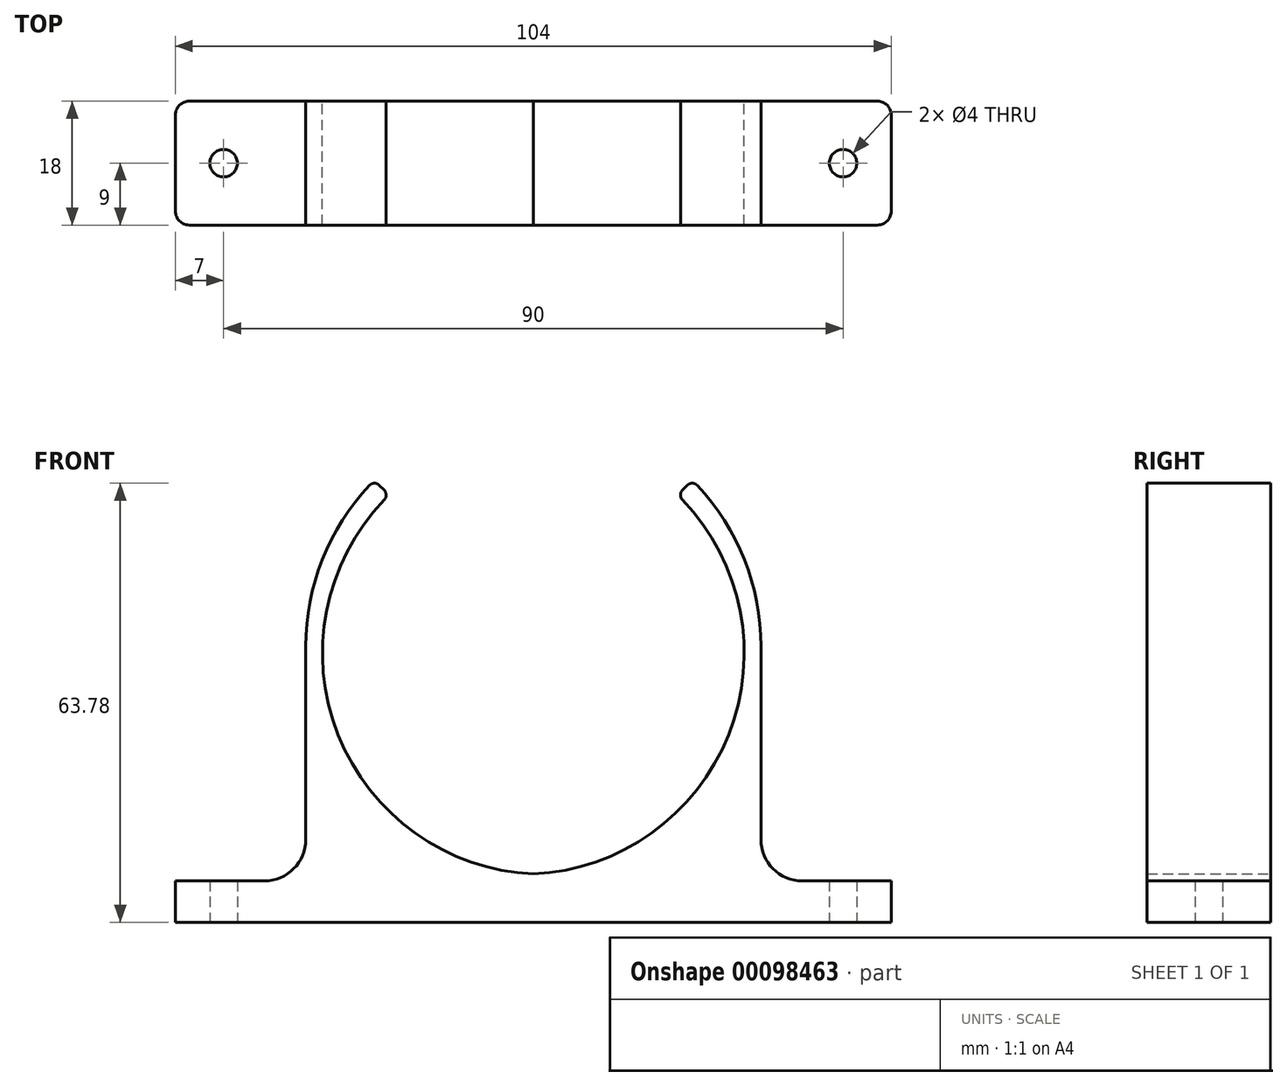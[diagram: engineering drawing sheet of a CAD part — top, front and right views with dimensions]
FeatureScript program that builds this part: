
annotation { "Feature Type Name" : "Feature", "Feature Type Description" : "" }
export const myFeature = defineFeature(function(context is Context, id is Id, definition is map)
    precondition{}
    {
        {
            var Q0;
            Q0=qCreatedBy(makeId("Front.planeOp"),FACE);
            var sketch = newSketch(context, id + "F0", { "sketchPlane" : qUnion([Q0])});
            skCircle(sketch, "E0", {"center": v(0, 0) * mm, "radius": 32.1 * mm, "construction": true});
            skCircle(sketch, "E1.0", {"center": v(0, 0) * mm, "radius": 34.1 * mm, "construction": true});
            skCircle(sketch, "E2.0", {"center": v(0, 0) * mm, "radius": 30.1 * mm, "construction": true});
            skArc(sketch, "E3", {"start": v(0, -34.1) * mm, "mid": v(28.36, -13.9) * mm, "end": v(21.66, 20.28) * mm});
            skLineSegment(sketch, "E4", {"start": v(20.97, 20.97) * mm, "end": v(21.28, 21.28) * mm, "construction": true});
            skPoint(sketch, "E5.orphan", {"position": v(0, 30.1) * mm});
            skLineSegment(sketch, "E6", {"start": v(33.07, -35.1) * mm, "end": v(52, -35.1) * mm});
            skLineSegment(sketch, "E7", {"start": v(52, -35.1) * mm, "end": v(52, -41.1) * mm});
            skLineSegment(sketch, "E8", {"start": v(52, -41.1) * mm, "end": v(0, -41.1) * mm});
            skLineSegment(sketch, "E9", {"start": v(33.07, -1) * mm, "end": v(33.07, -35.1) * mm});
            skArc(sketch, "E10.trimOffspring", {"start": v(33.07, -1) * mm, "mid": v(30.68, 11.56) * mm, "end": v(23.82, 22.36) * mm});
            skPoint(sketch, "E11.visualSharp", {"position": v(20.97, 20.97) * mm});
            skArc(sketch, "E11.filletArc", {"start": v(21.68, 21.68) * mm, "mid": v(21.38, 20.98) * mm, "end": v(21.66, 20.28) * mm});
            skPoint(sketch, "E12.visualSharp", {"position": v(23.1, 23.1) * mm});
            skArc(sketch, "E12.filletArc", {"start": v(23.82, 22.36) * mm, "mid": v(23.1, 22.68) * mm, "end": v(22.38, 22.38) * mm});
            skLineSegment(sketch, "E13", {"start": v(21.68, 21.68) * mm, "end": v(22.38, 22.38) * mm});
            skPoint(sketch, "E14.orphan", {"position": v(32.57, -6.82) * mm});
            skPoint(sketch, "E15.MirrorCS.end.orphan", {"position": v(0, -41.1) * mm});
            skPoint(sketch, "E16.MirrorCS.start.orphan", {"position": v(0, -34.1) * mm});
            skArc(sketch, "E17.MirrorCS", {"start": v(0, -34.1) * mm, "mid": v(-28.36, -13.9) * mm, "end": v(-21.66, 20.28) * mm});
            skArc(sketch, "E18.MirrorCS", {"start": v(-21.68, 21.68) * mm, "mid": v(-21.38, 20.98) * mm, "end": v(-21.66, 20.28) * mm});
            skLineSegment(sketch, "E19.MirrorCS", {"start": v(-21.68, 21.68) * mm, "end": v(-22.38, 22.38) * mm});
            skArc(sketch, "E20.MirrorCS", {"start": v(-23.82, 22.36) * mm, "mid": v(-23.1, 22.68) * mm, "end": v(-22.38, 22.38) * mm});
            skArc(sketch, "E21.MirrorCS", {"start": v(-33.07, -1) * mm, "mid": v(-30.68, 11.56) * mm, "end": v(-23.82, 22.36) * mm});
            skLineSegment(sketch, "E22.MirrorCS", {"start": v(-33.07, -1) * mm, "end": v(-33.07, -35.1) * mm});
            skLineSegment(sketch, "E23.MirrorCS", {"start": v(-33.07, -35.1) * mm, "end": v(-52, -35.1) * mm});
            skLineSegment(sketch, "E24.MirrorCS", {"start": v(-52, -35.1) * mm, "end": v(-52, -41.1) * mm});
            skLineSegment(sketch, "E25.MirrorCS", {"start": v(-52, -41.1) * mm, "end": v(0, -41.1) * mm});
            skSolve(sketch);
        }
        {
            var Q0;
            Q0 = qSketchRegion(id + "F0", true);
            extrude(context, id + "F1", {"entities" : qUnion([Q0]), "depth" : 18 * mm});
        }
        {
            var Q0;
            Q0=makeQuery(id+"F1.opExtrude","SWEPT_FACE",FACE,{"disambiguationData":[OSD([sQuery(id+"F0.wireOp",EDGE,"E8"),sQuery(id+"F0.wireOp",EDGE,"E15.MirrorCS")])]});
            var sketch = newSketch(context, id + "F2", { "sketchPlane" : qUnion([Q0])});
            skLineSegment(sketch, "E26", {"start": v(52, 9) * mm, "end": v(-48, 9) * mm, "construction": true});
            skCircle(sketch, "E27", {"center": v(-45, 9) * mm, "radius": 2 * mm});
            skCircle(sketch, "E28.MirrorC", {"center": v(45, 9) * mm, "radius": 2 * mm});
            skSolve(sketch);
        }
        {
            var Q0;
            Q0 = qSketchRegion(id + "F2", true);
            extrude(context, id + "F3", {"entities" : qUnion([Q0]), "operationType" : NewBodyOperationType.REMOVE, "endBound" : BoundingType.UP_TO_NEXT, "oppositeDirection" : true, "depth" : 25 * mm});
        }
        {
            var Q0;
            Q0=makeQuery(id+"F1.opExtrude","CAP_EDGE",EDGE,{"disambiguationData":[OSD([sQuery(id+"F0.wireOp",EDGE,"E24.MirrorCS")])],"isStart":true});
            var Q1;
            Q1=makeQuery(id+"F1.opExtrude","CAP_EDGE",EDGE,{"disambiguationData":[OSD([sQuery(id+"F0.wireOp",EDGE,"E24.MirrorCS")])],"isStart":false});
            var Q2;
            Q2=makeQuery(id+"F1.opExtrude","CAP_EDGE",EDGE,{"disambiguationData":[OSD([sQuery(id+"F0.wireOp",EDGE,"E7")])],"isStart":false});
            var Q3;
            Q3=makeQuery(id+"F1.opExtrude","CAP_EDGE",EDGE,{"disambiguationData":[OSD([sQuery(id+"F0.wireOp",EDGE,"E7")])],"isStart":true});
            fillet(context, id + "F4", {"entities" : qUnion([Q0, Q1, Q2, Q3]), "radius" : 2 * mm, "tangentPropagation" : true, "allowEdgeOverflow" : false});
        }
        {
            var Q0;
            Q0=makeQuery(id+"F1.opExtrude","SWEPT_EDGE",EDGE,{"disambiguationData":[OSD([sQuery(id+"F0.wireOp",EDGE,"E22.MirrorCS"),sQuery(id+"F0.wireOp",EDGE,"E23.MirrorCS")])]});
            var Q1;
            Q1=makeQuery(id+"F1.opExtrude","SWEPT_EDGE",EDGE,{"disambiguationData":[OSD([sQuery(id+"F0.wireOp",EDGE,"E6"),sQuery(id+"F0.wireOp",EDGE,"E9")])]});
            fillet(context, id + "F5", {"entities" : qUnion([Q0, Q1]), "radius" : 6 * mm, "tangentPropagation" : true, "allowEdgeOverflow" : false});
        }
    });
